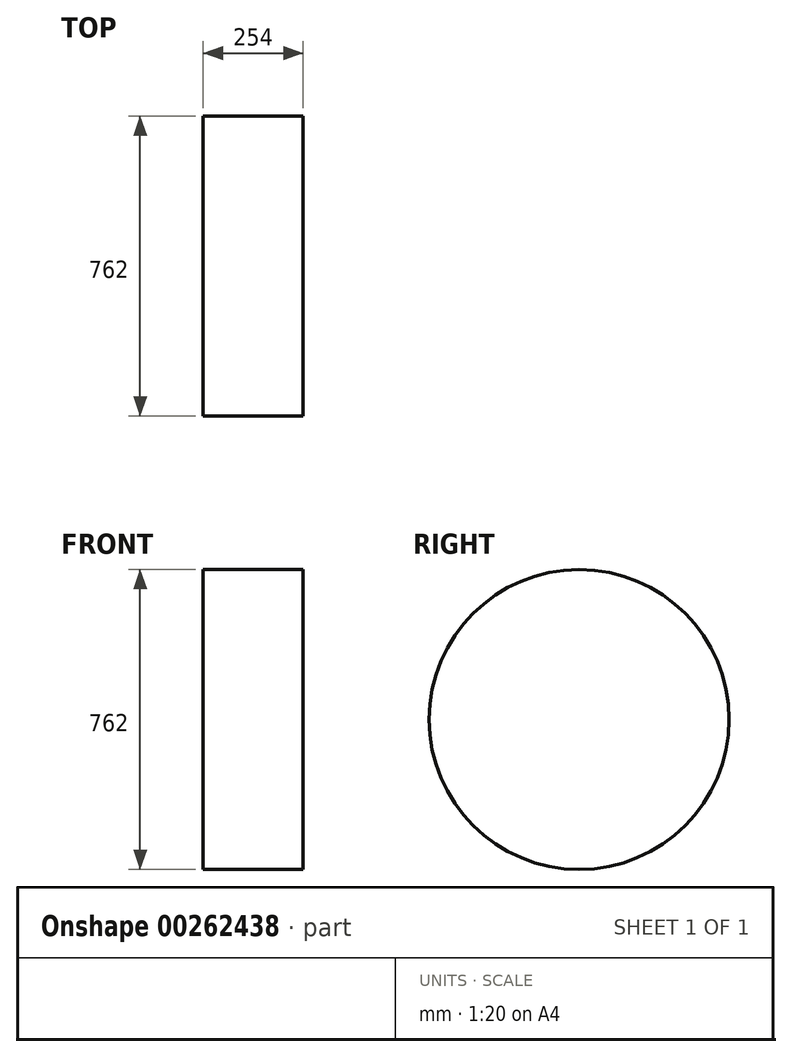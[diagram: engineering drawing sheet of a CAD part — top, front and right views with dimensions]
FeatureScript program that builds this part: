
annotation { "Feature Type Name" : "Feature", "Feature Type Description" : "" }
export const myFeature = defineFeature(function(context is Context, id is Id, definition is map)
    precondition{}
    {
        {
            var Q0;
            Q0=qCreatedBy(makeId("Right.planeOp"),FACE);
            var sketch = newSketch(context, id + "F0", { "sketchPlane" : qUnion([Q0])});
            skCircle(sketch, "E0", {"center": v(0, 0) * mm, "radius": 381 * mm});
            skSolve(sketch);
        }
        {
            var Q0;
            Q0 = qSketchRegion(id + "F0", true);
            extrude(context, id + "F1", {"entities" : qUnion([Q0]), "depth" : 254 * mm});
        }
    });
